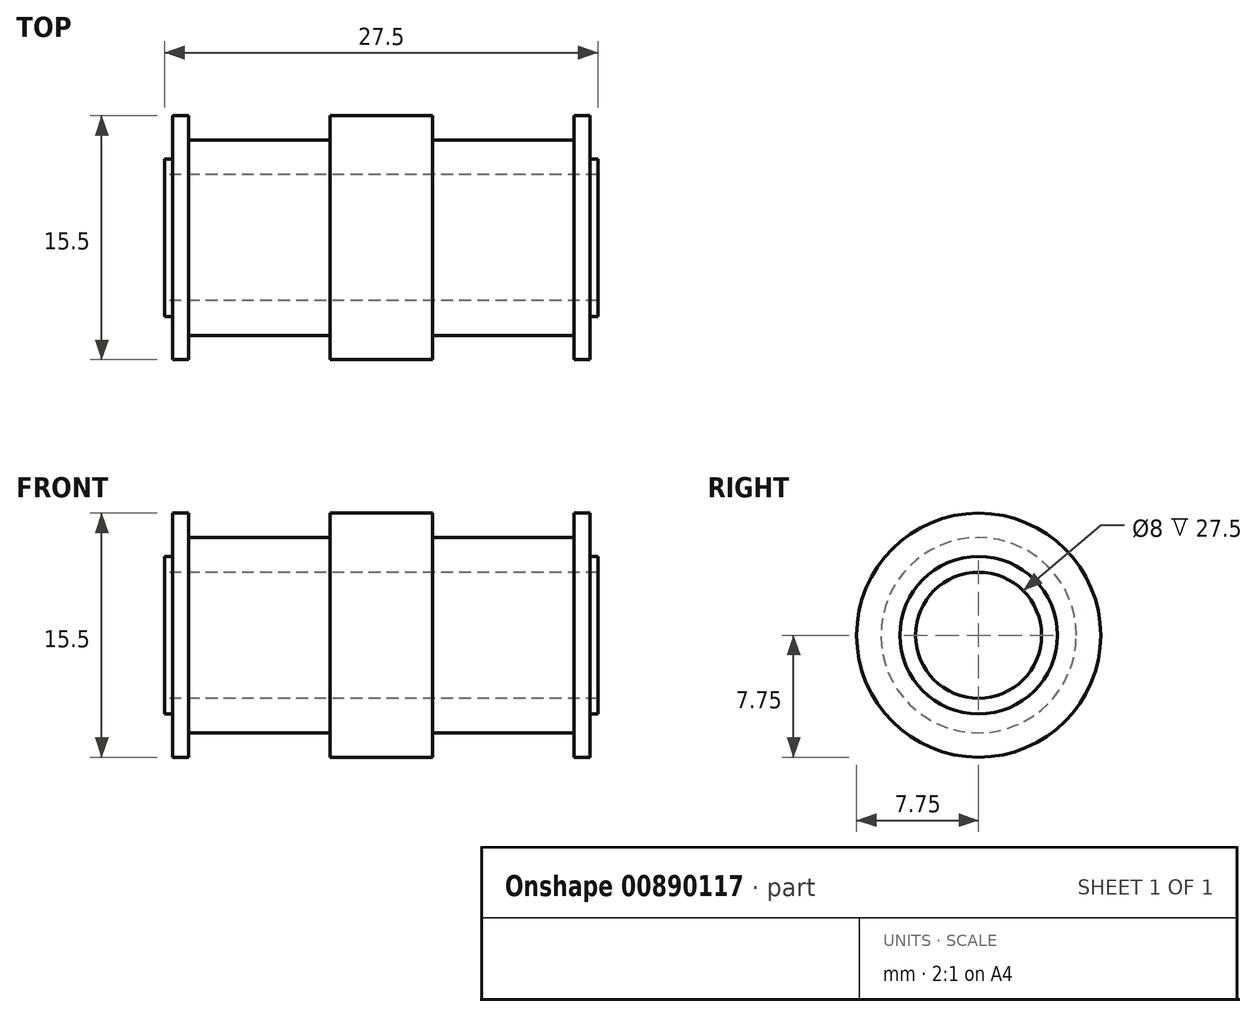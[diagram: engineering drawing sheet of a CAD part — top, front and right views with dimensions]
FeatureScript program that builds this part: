
annotation { "Feature Type Name" : "Feature", "Feature Type Description" : "" }
export const myFeature = defineFeature(function(context is Context, id is Id, definition is map)
    precondition{}
    {
        {
            var Q0;
            Q0=qCreatedBy(makeId("Right.planeOp"),FACE);
            var sketch = newSketch(context, id + "F0", { "sketchPlane" : qUnion([Q0])});
            skCircle(sketch, "E0", {"center": v(0, 0) * mm, "radius": 5 * mm});
            skCircle(sketch, "E1", {"center": v(0, 0) * mm, "radius": 4 * mm});
            skSolve(sketch);
        }
        {
            var Q0;
            Q0=qSketchRegion(id+"F0",true);
            extrude(context, id + "F1", {"entities" : qUnion([Q0]), "depth" : 0.5 * mm, "offsetDistance" : 25 * mm});
        }
        {
            var Q0;
            Q0=makeQuery(id+"F1.opExtrude","CAP_FACE",FACE,{"disambiguationData":[OSD([sQuery(id+"F0.wireOp",EDGE,"E0"),sQuery(id+"F0.wireOp",EDGE,"E1")])],"isStart":false});
            var sketch = newSketch(context, id + "F2", { "sketchPlane" : qUnion([Q0])});
            skCircle(sketch, "E2", {"center": v(0, 0) * mm, "radius": 7.75 * mm});
            skSolve(sketch);
        }
        {
            var Q0;
            Q0=makeQuery(id+"F2.imprint","IMPRINT",FACE,{"disambiguationData":[TD([[makeQuery(id+"F2.imprint","IMPRINT",EDGE,{"derivedFrom":sQuery(id+"F2.wireOp",EDGE,"E2")}),1.0]])]});
            var Q1;
            Q1=makeQuery(id+"F2.imprint","IMPRINT",FACE,{"disambiguationData":[TD([[makeQuery(id+"F2.imprint","IMPRINT",EDGE,{"derivedFrom":makeQuery(id+"F1.opExtrude","CAP_EDGE",EDGE,{"disambiguationData":[OSD([sQuery(id+"F0.wireOp",EDGE,"E0")])],"isStart":false})}),1.0]])]});
            extrude(context, id + "F3", {"entities" : qUnion([Q0, Q1]), "depth" : 1 * mm, "offsetDistance" : 25 * mm});
        }
        {
            var Q0;
            Q0=makeQuery(id+"F3.opExtrude","CAP_FACE",FACE,{"disambiguationData":[OSD([sQuery(id+"F0.wireOp",EDGE,"E1"),sQuery(id+"F2.wireOp",EDGE,"E2")])],"isStart":false});
            var sketch = newSketch(context, id + "F4", { "sketchPlane" : qUnion([Q0])});
            skCircle(sketch, "E3", {"center": v(0, 0) * mm, "radius": 6.2 * mm});
            skSolve(sketch);
        }
        {
            var Q0;
            Q0=makeQuery(id+"F4.imprint","IMPRINT",FACE,{"disambiguationData":[TD([[makeQuery(id+"F4.imprint","IMPRINT",EDGE,{"derivedFrom":sQuery(id+"F4.wireOp",EDGE,"E3")}),1.0]])]});
            extrude(context, id + "F5", {"entities" : qUnion([Q0]), "operationType" : NewBodyOperationType.ADD, "depth" : 9 * mm, "offsetDistance" : 25 * mm});
        }
        {
            var Q0;
            Q0=makeQuery(id+"F5.opExtrude","CAP_FACE",FACE,{"disambiguationData":[OSD([sQuery(id+"F0.wireOp",EDGE,"E1"),sQuery(id+"F4.wireOp",EDGE,"E3")])],"isStart":false});
            var sketch = newSketch(context, id + "F6", { "sketchPlane" : qUnion([Q0])});
            skCircle(sketch, "E4", {"center": v(0, 0) * mm, "radius": 4 * mm});
            skCircle(sketch, "E5", {"center": v(0, 0) * mm, "radius": 7.75 * mm});
            skSolve(sketch);
        }
        {
            var Q0;
            Q0=qSketchRegion(id+"F6",true);
            extrude(context, id + "F7", {"entities" : qUnion([Q0]), "depth" : 3.25 * mm, "offsetDistance" : 25 * mm});
        }
        {
            var Q0;
            Q0=makeQuery(id+"F3.opExtrude","SWEPT_BODY",BODY,{"disambiguationData":[OSD([sQuery(id+"F0.wireOp",EDGE,"E1"),sQuery(id+"F2.wireOp",EDGE,"E2")])]});
            var Q1;
            Q1=makeQuery(id+"F1.opExtrude","SWEPT_BODY",BODY,{"disambiguationData":[OSD([sQuery(id+"F0.wireOp",EDGE,"E0"),sQuery(id+"F0.wireOp",EDGE,"E1")])]});
            var Q2;
            Q2=makeQuery(id+"F7.opExtrude","SWEPT_BODY",BODY,{"disambiguationData":[OSD([sQuery(id+"F6.wireOp",EDGE,"E4"),sQuery(id+"F6.wireOp",EDGE,"E5")])]});
            var Q3;
            Q3=makeQuery(id+"F7.opExtrude","CAP_FACE",FACE,{"disambiguationData":[OSD([sQuery(id+"F6.wireOp",EDGE,"E4"),sQuery(id+"F6.wireOp",EDGE,"E5")])],"isStart":false});
            mirror(context, id + "F8", {"operationType" : NewBodyOperationType.ADD, "entities" : qUnion([Q0, Q1, Q2]), "mirrorPlane" : qUnion([Q3])});
        }
    });
